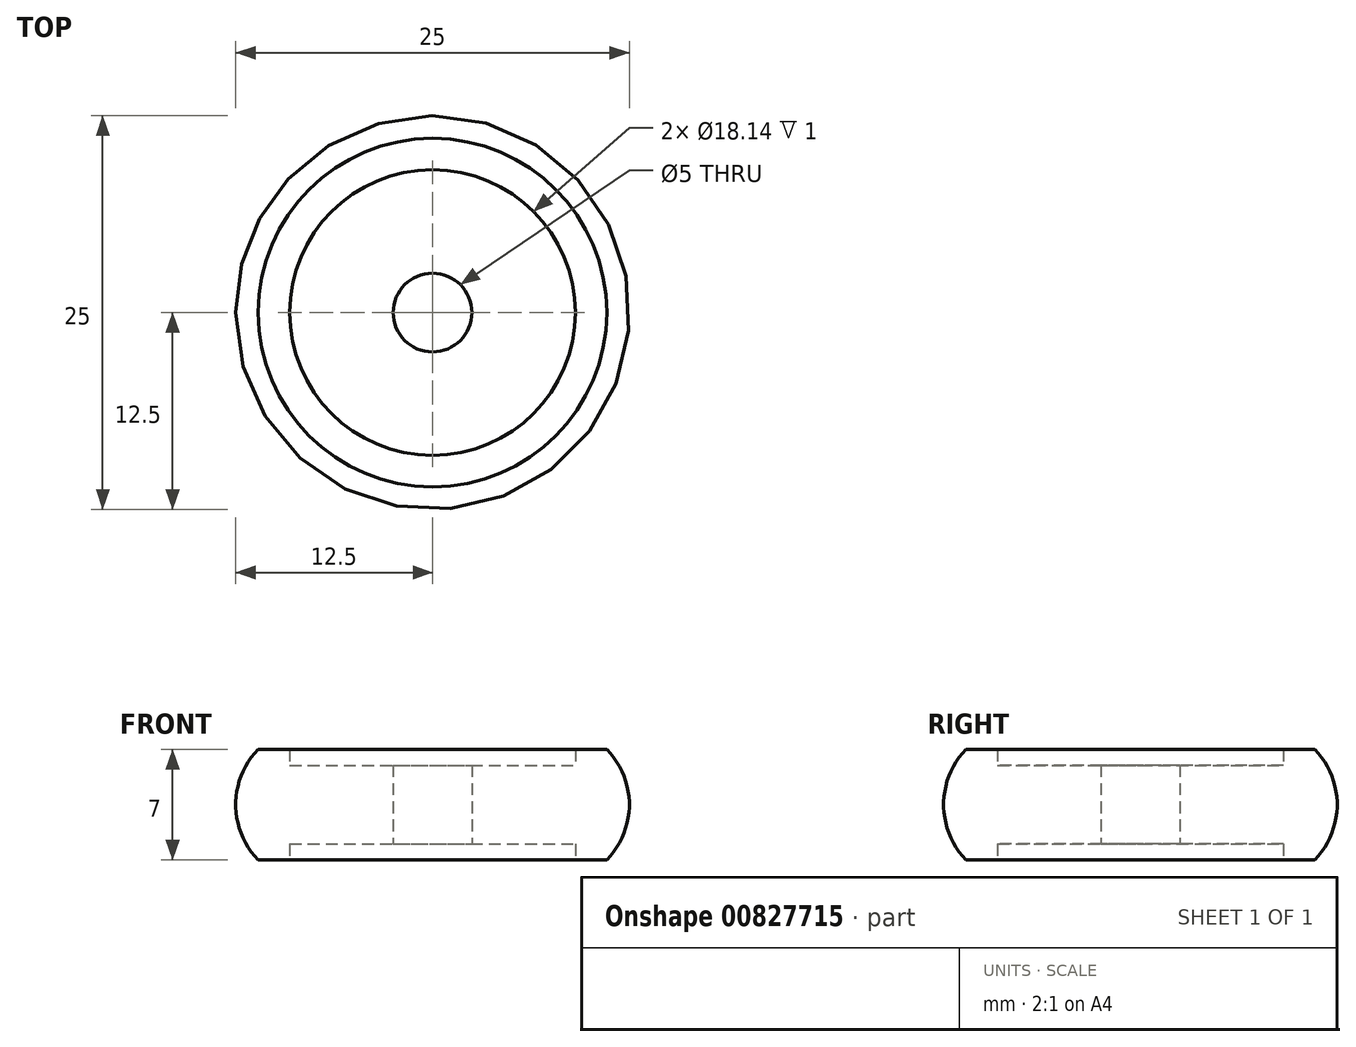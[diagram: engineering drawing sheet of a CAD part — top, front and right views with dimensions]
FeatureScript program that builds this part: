
annotation { "Feature Type Name" : "Feature", "Feature Type Description" : "" }
export const myFeature = defineFeature(function(context is Context, id is Id, definition is map)
    precondition{}
    {
        {
            var Q0;
            Q0=qCreatedBy(makeId("Front.planeOp"),FACE);
            var sketch = newSketch(context, id + "F0", { "sketchPlane" : qUnion([Q0])});
            skLineSegment(sketch, "E0", {"start": v(0, 0) * mm, "end": v(2.5, 0) * mm, "construction": true});
            skArc(sketch, "E1", {"start": v(12.5, 0) * mm, "mid": v(12.13, 1.9) * mm, "end": v(11.07, 3.5) * mm});
            skLineSegment(sketch, "E2", {"start": v(0, 0) * mm, "end": v(0, 8.5) * mm});
            skLineSegment(sketch, "E3", {"start": v(11.07, 3.5) * mm, "end": v(9.07, 3.5) * mm});
            skLineSegment(sketch, "E4", {"start": v(9.07, 3.5) * mm, "end": v(9.07, 2.5) * mm});
            skLineSegment(sketch, "E5", {"start": v(9.07, 2.5) * mm, "end": v(2.5, 2.5) * mm});
            skLineSegment(sketch, "E6", {"start": v(2.5, 2.5) * mm, "end": v(2.5, 0) * mm});
            skLineSegment(sketch, "E7.MirrorCS", {"start": v(2.5, -2.5) * mm, "end": v(2.5, 0) * mm});
            skLineSegment(sketch, "E8.MirrorCS", {"start": v(9.07, -2.5) * mm, "end": v(2.5, -2.5) * mm});
            skLineSegment(sketch, "E9.MirrorCS", {"start": v(9.07, -3.5) * mm, "end": v(9.07, -2.5) * mm});
            skLineSegment(sketch, "E10.MirrorCS", {"start": v(11.07, -3.5) * mm, "end": v(9.07, -3.5) * mm});
            skArc(sketch, "E11.MirrorCS", {"start": v(12.5, 0) * mm, "mid": v(12.13, -1.9) * mm, "end": v(11.07, -3.5) * mm});
            skSolve(sketch);
        }
        {
            var Q0;
            Q0 = qSketchRegion(id + "F0", true);
            var Q1;
            Q1=sQuery(id+"F0.wireOp",EDGE,"E2");
            revolve(context, id + "F1", {"surfaceOperationType" : NewSurfaceOperationType.NEW, "entities" : qUnion([Q0]), "axis" : qUnion([Q1]), "revolveType" : RevolveType.FULL});
        }
    });
